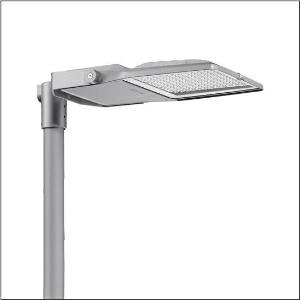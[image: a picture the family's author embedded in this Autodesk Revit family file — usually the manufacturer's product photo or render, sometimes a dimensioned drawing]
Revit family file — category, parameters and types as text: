
# Revit family: floodlight_fl_21_iq_midi___pl61_5xa7782f2c3a_b633
name_source: partatom
category: Lighting Fixtures
units: mm (PartAtom-declared; Revit-internal decimal feet)

## family parameters
Cut with Voids When Loaded = No
Host = Face
Light Source = No
Part Type = Normal
Room Calculation Point = No
Round Connector Dimension = Use Diameter
Shared = No

## types (1)
- --- (1 x LED, 35100 lm, 270.2 W, 3000K)
    Apparent Load = 270 VA
    CIE Flux Codes = 33 65 98 100 100
    Color Rendering = 70
    Color Temperature = 3000K
    Default Elevation = 1800 mm
    Description = Floodlight FL 21 iQ midi, floodlight, primary light control with lens, of PMMA, primary optical cover: protective disc, of toughened safety glass, transparent, light distribution: PL61, light emission: direct distribution, installation type: surface-mounted, LED, High Power LED, rated luminous flux: 35.100lm, luminous efficacy: 130lm/W, light colour: 730, colour temperature: 3000K, control gear: ECG iQ, control: optimised constant luminous flux control (CLO 2.0), Desk-Remote (wireless, voltage-free reading and setting of iQ features in the workshop via application-optimized NFC function/RFID function), Smart-Wire, Night-Set, Temp-Guard, Auto-Match, Street-Remote, with terminal, 6-pole, mains connection: 220..240V, AC, 50/60Hz, start of lifetime: 270W, end of service life: 287W, reduction: 117W, luminaire housing, of diecast aluminium, powder-coated, Siteco® metallic grey (DB 702S), corrosivity category C5 mid according to DIN EN ISO 12944, sealing non-destructively replaceable, please order mast flange separately, mast bracket, of steel, galvanised, powder-coated, Siteco® metallic grey (DB 702S), protection rating (complete): IP66, insulation class (complete): insulation class II (safety insulation), certification: CE, protection symbol: D, impact resistance: IK08, permissible operating ambient temperature: -40..+40°C, permissible operating ambient temperature for outdoor applications: -40..+50°C, standard: DIN EN 12944, LABS conformity tested according to VDMA 24364:2018-05, packaging unit: 1 piece

Light Distribution: PL61
    Height = 76 mm
    Lamp = 1 x LED
    Lamp Light Flux = 35100 lm
    Lamp Power = 270.2 W
    Lamp count = 1
    Length = 657 mm
    Luminous efficacy = 130 lm/W
    Manufacturer = Siteco
    ModVariant = No
    Model = 5XA7782F2C3A
    Number of Poles = 1
    OnlyDefault = Yes
    Power Factor = 1
    Product Name = Floodlight FL 21 iQ midi | PL61
    Product group = floodlight | pylon annexe
    ProductGroupID = 6200
    Protection Class = Protection class II
    Protection Degree = IP 66
    RLX_Detail_Level = 1
    RLX_Emergency_Light_Flux = 0 lm
    RLX_Emergency_Type = 0
    RLX_Emergency_Type_DB = No
    RlxData = <blob elided: 153589 chars, md5=16322efe>
    Socket = socket
    Standby Power = 0 W
    System Light Flux = 35100 lm
    System Power = 270 W
    Type Comments = factory setting: luminous flux: 100 % | dim-lin: 254 | 620 mA
    Type Image = l_1007123.jpg
    URL = http://relux.com
    VarID = @adj_056583
    Voltage = 0 V
    Weight = 0.00 kg
    Width = 442 mm

## geometry (parser evidence)
native form markers: Blend x4, Sweep x12
no freeform markers — native parametric forms only
